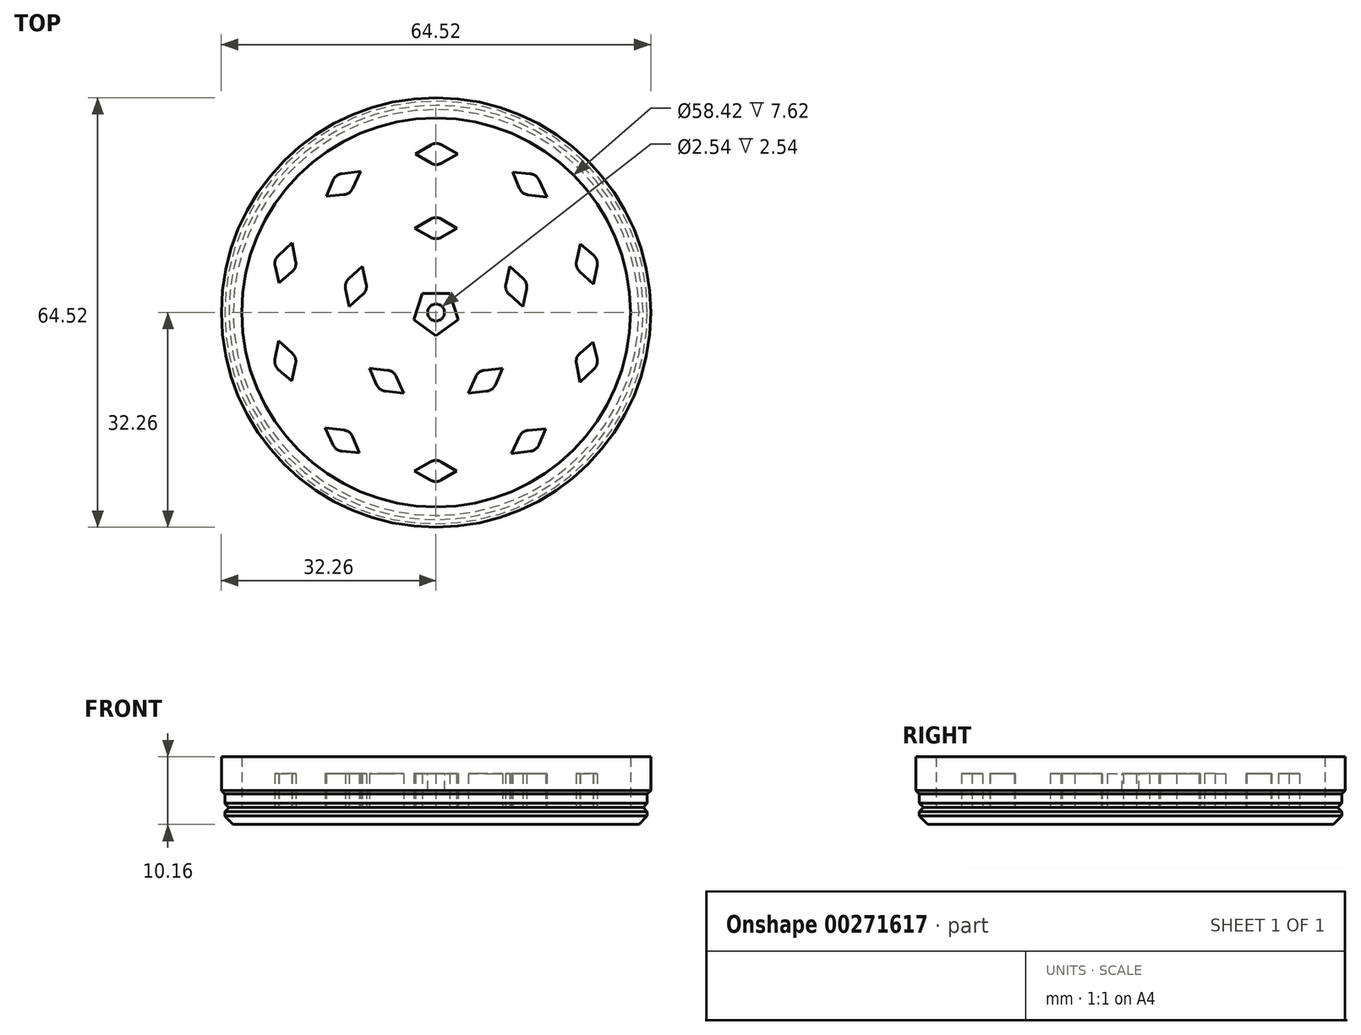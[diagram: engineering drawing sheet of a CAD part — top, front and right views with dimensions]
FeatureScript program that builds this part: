
annotation { "Feature Type Name" : "Feature", "Feature Type Description" : "" }
export const myFeature = defineFeature(function(context is Context, id is Id, definition is map)
    precondition{}
    {
        {
            var Q0;
            Q0=qCreatedBy(makeId("Front.planeOp"),FACE);
            var sketch = newSketch(context, id + "F0", { "sketchPlane" : qUnion([Q0])});
            skLineSegment(sketch, "E0", {"start": v(0, 0) * mm, "end": v(0, 32.12) * mm, "construction": true});
            skLineSegment(sketch, "E1", {"start": v(0, 0) * mm, "end": v(31.75, 0) * mm});
            skLineSegment(sketch, "E2", {"start": v(31.75, 0) * mm, "end": v(31.75, 1.9) * mm});
            skLineSegment(sketch, "E3", {"start": v(31.75, 10.16) * mm, "end": v(29.21, 10.16) * mm});
            skLineSegment(sketch, "E4", {"start": v(29.21, 10.16) * mm, "end": v(29.21, 2.54) * mm});
            skLineSegment(sketch, "E5", {"start": v(29.21, 2.54) * mm, "end": v(0, 2.54) * mm});
            skLineSegment(sketch, "E6", {"start": v(0, 2.54) * mm, "end": v(0, 0) * mm});
            skLineSegment(sketch, "E7.bottom", {"start": v(31.75, 10.16) * mm, "end": v(32.26, 10.16) * mm});
            skLineSegment(sketch, "E7.top", {"start": v(31.75, 5.08) * mm, "end": v(32.26, 5.08) * mm});
            skLineSegment(sketch, "E7.left", {"start": v(31.75, 10.16) * mm, "end": v(31.75, 5.08) * mm});
            skLineSegment(sketch, "E7.right", {"start": v(32.26, 10.16) * mm, "end": v(32.26, 5.08) * mm});
            skLineSegment(sketch, "E8", {"start": v(31.75, 3.18) * mm, "end": v(31.12, 2.54) * mm});
            skLineSegment(sketch, "E9", {"start": v(31.12, 2.54) * mm, "end": v(31.75, 1.9) * mm});
            skLineSegment(sketch, "E10.trimOffspring", {"start": v(31.75, 3.17) * mm, "end": v(31.75, 10.16) * mm});
            skLineSegment(sketch, "E11", {"start": v(32.26, 5.08) * mm, "end": v(31.75, 4.57) * mm});
            skSolve(sketch);
        }
        {
            var Q0;
            Q0 = qSketchRegion(id + "F0", true);
            var Q1;
            Q1=sQuery(id+"F0.wireOp",EDGE,"E0");
            revolve(context, id + "F1", {"entities" : qUnion([Q0]), "axis" : qUnion([Q1]), "revolveType" : RevolveType.FULL});
        }
        {
            var Q0;
            Q0=qCreatedBy(makeId("Top.planeOp"),FACE);
            var sketch = newSketch(context, id + "F2", { "sketchPlane" : qUnion([Q0])});
            skLineSegment(sketch, "E12", {"start": v(-2.06, 2.86) * mm, "end": v(2.06, 2.86) * mm});
            skLineSegment(sketch, "E13", {"start": v(-2.06, 2.86) * mm, "end": v(-3.34, -1.07) * mm});
            skCircle(sketch, "E14", {"center": v(0, 0) * mm, "radius": 25.4 * mm, "construction": true});
            skLineSegment(sketch, "E15", {"start": v(-0.82, 25.17) * mm, "end": v(-3.08, 23.81) * mm});
            skLineSegment(sketch, "E16", {"start": v(-3.08, 23.81) * mm, "end": v(-0.8, 22.45) * mm});
            skLineSegment(sketch, "E17", {"start": v(0.79, 22.43) * mm, "end": v(3.27, 23.81) * mm});
            skLineSegment(sketch, "E18", {"start": v(3.27, 23.81) * mm, "end": v(0.77, 25.2) * mm});
            skArc(sketch, "E19.filletArc", {"start": v(0.77, 25.2) * mm, "mid": v(-0.03, 25.4) * mm, "end": v(-0.82, 25.17) * mm});
            skArc(sketch, "E20.filletArc", {"start": v(-0.8, 22.45) * mm, "mid": v(-0.01, 22.23) * mm, "end": v(0.79, 22.43) * mm});
            skLineSegment(sketch, "E21", {"start": v(-1.19, 22.23) * mm, "end": v(1.83, 22.23) * mm, "construction": true});
            skLineSegment(sketch, "E22", {"start": v(-1.91, 25.4) * mm, "end": v(1.92, 25.4) * mm, "construction": true});
            skLineSegment(sketch, "E23.1.0", {"start": v(-11.35, 21.19) * mm, "end": v(-14.2, 20.84) * mm});
            skLineSegment(sketch, "E23.1.1", {"start": v(-15.46, 19.89) * mm, "end": v(-16.49, 17.46) * mm});
            skArc(sketch, "E23.1.2", {"start": v(-14.2, 20.84) * mm, "mid": v(-14.95, 20.53) * mm, "end": v(-15.46, 19.89) * mm});
            skLineSegment(sketch, "E23.1.3", {"start": v(-16.49, 17.46) * mm, "end": v(-13.85, 17.7) * mm});
            skArc(sketch, "E23.1.4", {"start": v(-13.85, 17.7) * mm, "mid": v(-13.07, 17.97) * mm, "end": v(-12.55, 18.6) * mm});
            skLineSegment(sketch, "E23.1.5", {"start": v(-12.55, 18.6) * mm, "end": v(-11.35, 21.19) * mm});
            skLineSegment(sketch, "E23.2.0", {"start": v(-21.64, 10.47) * mm, "end": v(-23.73, 8.52) * mm});
            skLineSegment(sketch, "E23.2.1", {"start": v(-24.2, 7) * mm, "end": v(-23.6, 4.43) * mm});
            skArc(sketch, "E23.2.2", {"start": v(-23.73, 8.52) * mm, "mid": v(-24.17, 7.82) * mm, "end": v(-24.2, 7) * mm});
            skLineSegment(sketch, "E23.2.3", {"start": v(-23.6, 4.43) * mm, "end": v(-21.6, 6.17) * mm});
            skArc(sketch, "E23.2.4", {"start": v(-21.6, 6.17) * mm, "mid": v(-21.14, 6.86) * mm, "end": v(-21.09, 7.68) * mm});
            skLineSegment(sketch, "E23.2.5", {"start": v(-21.09, 7.68) * mm, "end": v(-21.64, 10.47) * mm});
            skLineSegment(sketch, "E23.3.0", {"start": v(-23.66, -4.25) * mm, "end": v(-24.2, -7.06) * mm});
            skLineSegment(sketch, "E23.3.1", {"start": v(-23.69, -8.56) * mm, "end": v(-21.7, -10.29) * mm});
            skArc(sketch, "E23.3.2", {"start": v(-24.2, -7.06) * mm, "mid": v(-24.15, -7.88) * mm, "end": v(-23.69, -8.56) * mm});
            skLineSegment(sketch, "E23.3.3", {"start": v(-21.7, -10.29) * mm, "end": v(-21.1, -7.7) * mm});
            skArc(sketch, "E23.3.4", {"start": v(-21.1, -7.7) * mm, "mid": v(-21.13, -6.88) * mm, "end": v(-21.57, -6.18) * mm});
            skLineSegment(sketch, "E23.3.5", {"start": v(-21.57, -6.18) * mm, "end": v(-23.66, -4.25) * mm});
            skLineSegment(sketch, "E23.4.0", {"start": v(-16.64, -17.34) * mm, "end": v(-15.44, -19.94) * mm});
            skLineSegment(sketch, "E23.4.1", {"start": v(-14.14, -20.85) * mm, "end": v(-11.5, -21.08) * mm});
            skArc(sketch, "E23.4.2", {"start": v(-15.44, -19.94) * mm, "mid": v(-14.9, -20.57) * mm, "end": v(-14.14, -20.85) * mm});
            skLineSegment(sketch, "E23.4.3", {"start": v(-11.5, -21.08) * mm, "end": v(-12.55, -18.64) * mm});
            skArc(sketch, "E23.4.4", {"start": v(-12.55, -18.64) * mm, "mid": v(-13.05, -17.99) * mm, "end": v(-13.82, -17.68) * mm});
            skLineSegment(sketch, "E23.4.5", {"start": v(-13.82, -17.68) * mm, "end": v(-16.64, -17.34) * mm});
            skLineSegment(sketch, "E23.5.0", {"start": v(-3.27, -23.81) * mm, "end": v(-0.77, -25.2) * mm});
            skLineSegment(sketch, "E23.5.1", {"start": v(0.82, -25.17) * mm, "end": v(3.08, -23.81) * mm});
            skArc(sketch, "E23.5.2", {"start": v(-0.77, -25.2) * mm, "mid": v(0.03, -25.4) * mm, "end": v(0.82, -25.17) * mm});
            skLineSegment(sketch, "E23.5.3", {"start": v(3.08, -23.81) * mm, "end": v(0.8, -22.45) * mm});
            skArc(sketch, "E23.5.4", {"start": v(0.8, -22.45) * mm, "mid": v(0.01, -22.23) * mm, "end": v(-0.79, -22.43) * mm});
            skLineSegment(sketch, "E23.5.5", {"start": v(-0.79, -22.43) * mm, "end": v(-3.27, -23.81) * mm});
            skLineSegment(sketch, "E23.6.0", {"start": v(11.35, -21.19) * mm, "end": v(14.2, -20.84) * mm});
            skLineSegment(sketch, "E23.6.1", {"start": v(15.46, -19.89) * mm, "end": v(16.49, -17.46) * mm});
            skArc(sketch, "E23.6.2", {"start": v(14.2, -20.84) * mm, "mid": v(14.95, -20.53) * mm, "end": v(15.46, -19.89) * mm});
            skLineSegment(sketch, "E23.6.3", {"start": v(16.49, -17.46) * mm, "end": v(13.85, -17.7) * mm});
            skArc(sketch, "E23.6.4", {"start": v(13.85, -17.7) * mm, "mid": v(13.07, -17.97) * mm, "end": v(12.55, -18.6) * mm});
            skLineSegment(sketch, "E23.6.5", {"start": v(12.55, -18.6) * mm, "end": v(11.35, -21.19) * mm});
            skLineSegment(sketch, "E23.7.0", {"start": v(21.64, -10.47) * mm, "end": v(23.73, -8.52) * mm});
            skLineSegment(sketch, "E23.7.1", {"start": v(24.2, -7) * mm, "end": v(23.6, -4.43) * mm});
            skArc(sketch, "E23.7.2", {"start": v(23.73, -8.52) * mm, "mid": v(24.17, -7.82) * mm, "end": v(24.2, -7) * mm});
            skLineSegment(sketch, "E23.7.3", {"start": v(23.6, -4.43) * mm, "end": v(21.6, -6.17) * mm});
            skArc(sketch, "E23.7.4", {"start": v(21.6, -6.17) * mm, "mid": v(21.14, -6.86) * mm, "end": v(21.09, -7.68) * mm});
            skLineSegment(sketch, "E23.7.5", {"start": v(21.09, -7.68) * mm, "end": v(21.64, -10.47) * mm});
            skLineSegment(sketch, "E23.8.0", {"start": v(23.66, 4.25) * mm, "end": v(24.2, 7.06) * mm});
            skLineSegment(sketch, "E23.8.1", {"start": v(23.69, 8.56) * mm, "end": v(21.7, 10.29) * mm});
            skArc(sketch, "E23.8.2", {"start": v(24.2, 7.06) * mm, "mid": v(24.15, 7.88) * mm, "end": v(23.69, 8.56) * mm});
            skLineSegment(sketch, "E23.8.3", {"start": v(21.7, 10.29) * mm, "end": v(21.1, 7.7) * mm});
            skArc(sketch, "E23.8.4", {"start": v(21.1, 7.7) * mm, "mid": v(21.13, 6.88) * mm, "end": v(21.57, 6.18) * mm});
            skLineSegment(sketch, "E23.8.5", {"start": v(21.57, 6.18) * mm, "end": v(23.66, 4.25) * mm});
            skLineSegment(sketch, "E23.9.0", {"start": v(16.64, 17.34) * mm, "end": v(15.44, 19.94) * mm});
            skLineSegment(sketch, "E23.9.1", {"start": v(14.14, 20.85) * mm, "end": v(11.5, 21.08) * mm});
            skArc(sketch, "E23.9.2", {"start": v(15.44, 19.94) * mm, "mid": v(14.9, 20.57) * mm, "end": v(14.14, 20.85) * mm});
            skLineSegment(sketch, "E23.9.3", {"start": v(11.5, 21.08) * mm, "end": v(12.55, 18.64) * mm});
            skArc(sketch, "E23.9.4", {"start": v(12.55, 18.64) * mm, "mid": v(13.05, 17.99) * mm, "end": v(13.82, 17.68) * mm});
            skLineSegment(sketch, "E23.9.5", {"start": v(13.82, 17.68) * mm, "end": v(16.64, 17.34) * mm});
            skLineSegment(sketch, "E24", {"start": v(3.17, 12.67) * mm, "end": v(-3.18, 12.67) * mm, "construction": true});
            skLineSegment(sketch, "E25", {"start": v(0, 12.67) * mm, "end": v(0, 0) * mm, "construction": true});
            skLineSegment(sketch, "E26", {"start": v(-3.18, 12.67) * mm, "end": v(-0.8, 11.3) * mm});
            skLineSegment(sketch, "E27", {"start": v(0.8, 11.3) * mm, "end": v(3.17, 12.67) * mm});
            skLineSegment(sketch, "E28", {"start": v(3.17, 12.67) * mm, "end": v(0.8, 14.04) * mm});
            skLineSegment(sketch, "E29", {"start": v(-0.8, 14.04) * mm, "end": v(-3.18, 12.67) * mm});
            skArc(sketch, "E30", {"start": v(0.8, 14.04) * mm, "mid": v(0, 14.26) * mm, "end": v(-0.8, 14.04) * mm});
            skArc(sketch, "E31", {"start": v(-0.8, 11.3) * mm, "mid": v(0, 11.08) * mm, "end": v(0.8, 11.3) * mm});
            skLineSegment(sketch, "E32.1.0", {"start": v(-11.07, 6.93) * mm, "end": v(-13.11, 5.1) * mm});
            skLineSegment(sketch, "E32.1.1", {"start": v(-10.5, 4.24) * mm, "end": v(-11.07, 6.93) * mm});
            skArc(sketch, "E32.1.2", {"start": v(-10.99, 2.73) * mm, "mid": v(-10.54, 3.42) * mm, "end": v(-10.5, 4.24) * mm});
            skLineSegment(sketch, "E32.1.3", {"start": v(-13.03, 0.9) * mm, "end": v(-10.99, 2.73) * mm});
            skLineSegment(sketch, "E32.1.4", {"start": v(-13.6, 3.58) * mm, "end": v(-13.03, 0.9) * mm});
            skArc(sketch, "E32.1.5", {"start": v(-13.11, 5.1) * mm, "mid": v(-13.56, 4.4) * mm, "end": v(-13.6, 3.58) * mm});
            skLineSegment(sketch, "E32.2.0", {"start": v(-10.01, -8.38) * mm, "end": v(-8.9, -10.9) * mm});
            skLineSegment(sketch, "E32.2.1", {"start": v(-7.28, -8.67) * mm, "end": v(-10.01, -8.38) * mm});
            skArc(sketch, "E32.2.2", {"start": v(-6, -9.6) * mm, "mid": v(-6.51, -8.96) * mm, "end": v(-7.28, -8.67) * mm});
            skLineSegment(sketch, "E32.2.3", {"start": v(-4.88, -12.12) * mm, "end": v(-6, -9.6) * mm});
            skLineSegment(sketch, "E32.2.4", {"start": v(-7.61, -11.83) * mm, "end": v(-4.88, -12.12) * mm});
            skArc(sketch, "E32.2.5", {"start": v(-8.9, -10.9) * mm, "mid": v(-8.38, -11.53) * mm, "end": v(-7.61, -11.83) * mm});
            skLineSegment(sketch, "E32.3.0", {"start": v(4.88, -12.12) * mm, "end": v(7.61, -11.83) * mm});
            skLineSegment(sketch, "E32.3.1", {"start": v(6, -9.6) * mm, "end": v(4.88, -12.12) * mm});
            skArc(sketch, "E32.3.2", {"start": v(7.28, -8.67) * mm, "mid": v(6.51, -8.96) * mm, "end": v(6, -9.6) * mm});
            skLineSegment(sketch, "E32.3.3", {"start": v(10.01, -8.38) * mm, "end": v(7.28, -8.67) * mm});
            skLineSegment(sketch, "E32.3.4", {"start": v(8.9, -10.9) * mm, "end": v(10.01, -8.38) * mm});
            skArc(sketch, "E32.3.5", {"start": v(7.61, -11.83) * mm, "mid": v(8.38, -11.53) * mm, "end": v(8.9, -10.9) * mm});
            skLineSegment(sketch, "E32.4.0", {"start": v(13.03, 0.9) * mm, "end": v(13.6, 3.58) * mm});
            skLineSegment(sketch, "E32.4.1", {"start": v(10.99, 2.73) * mm, "end": v(13.03, 0.9) * mm});
            skArc(sketch, "E32.4.2", {"start": v(10.5, 4.24) * mm, "mid": v(10.54, 3.42) * mm, "end": v(10.99, 2.73) * mm});
            skLineSegment(sketch, "E32.4.3", {"start": v(11.07, 6.93) * mm, "end": v(10.5, 4.24) * mm});
            skLineSegment(sketch, "E32.4.4", {"start": v(13.11, 5.1) * mm, "end": v(11.07, 6.93) * mm});
            skArc(sketch, "E32.4.5", {"start": v(13.6, 3.58) * mm, "mid": v(13.56, 4.4) * mm, "end": v(13.11, 5.1) * mm});
            skLineSegment(sketch, "E33", {"start": v(2.06, 2.86) * mm, "end": v(3.34, -1.07) * mm});
            skLineSegment(sketch, "E34", {"start": v(3.34, -1.07) * mm, "end": v(0, -3.5) * mm});
            skLineSegment(sketch, "E35", {"start": v(0, -3.5) * mm, "end": v(-3.34, -1.07) * mm});
            skSolve(sketch);
        }
        {
            var Q0;
            Q0 = qSketchRegion(id + "F2", true);
            extrude(context, id + "F3", {"entities" : qUnion([Q0]), "operationType" : NewBodyOperationType.ADD, "depth" : 7.62 * mm});
        }
        {
            var Q0;
            Q0 = qSketchRegion(id + "F2", true);
            extrude(context, id + "F4", {"entities" : qUnion([Q0]), "operationType" : NewBodyOperationType.ADD, "depth" : 7.62 * mm});
        }
        {
            var Q0;
            Q0=makeQuery(id+"F1.opRevolve","SWEPT_EDGE",EDGE,{"disambiguationData":[OSD([sQuery(id+"F0.wireOp",EDGE,"E1"),sQuery(id+"F0.wireOp",EDGE,"E2")])]});
            chamfer(context, id + "F5", {"entities" : qUnion([Q0]), "chamferType" : ChamferType.OFFSET_ANGLE, "width" : 1.27 * mm, "oppositeDirection" : false, "angle" : 45 * degree, "tangentPropagation" : true});
        }
        {
            var Q0;
            Q0=makeQuery(id+"F3.opExtrude","CAP_FACE",FACE,{"disambiguationData":[OSD([sQuery(id+"F2.wireOp",EDGE,"E12"),sQuery(id+"F2.wireOp",EDGE,"E13"),sQuery(id+"F2.wireOp",EDGE,"E33"),sQuery(id+"F2.wireOp",EDGE,"E34"),sQuery(id+"F2.wireOp",EDGE,"E35")])],"isStart":false});
            var sketch = newSketch(context, id + "F6", { "sketchPlane" : qUnion([Q0])});
            skCircle(sketch, "E36", {"center": v(0, 0) * mm, "radius": 1.27 * mm});
            skSolve(sketch);
        }
        {
            var Q0;
            Q0 = qSketchRegion(id + "F6", true);
            extrude(context, id + "F7", {"entities" : qUnion([Q0]), "operationType" : NewBodyOperationType.REMOVE, "oppositeDirection" : true, "depth" : 2.54 * mm});
        }
    });
